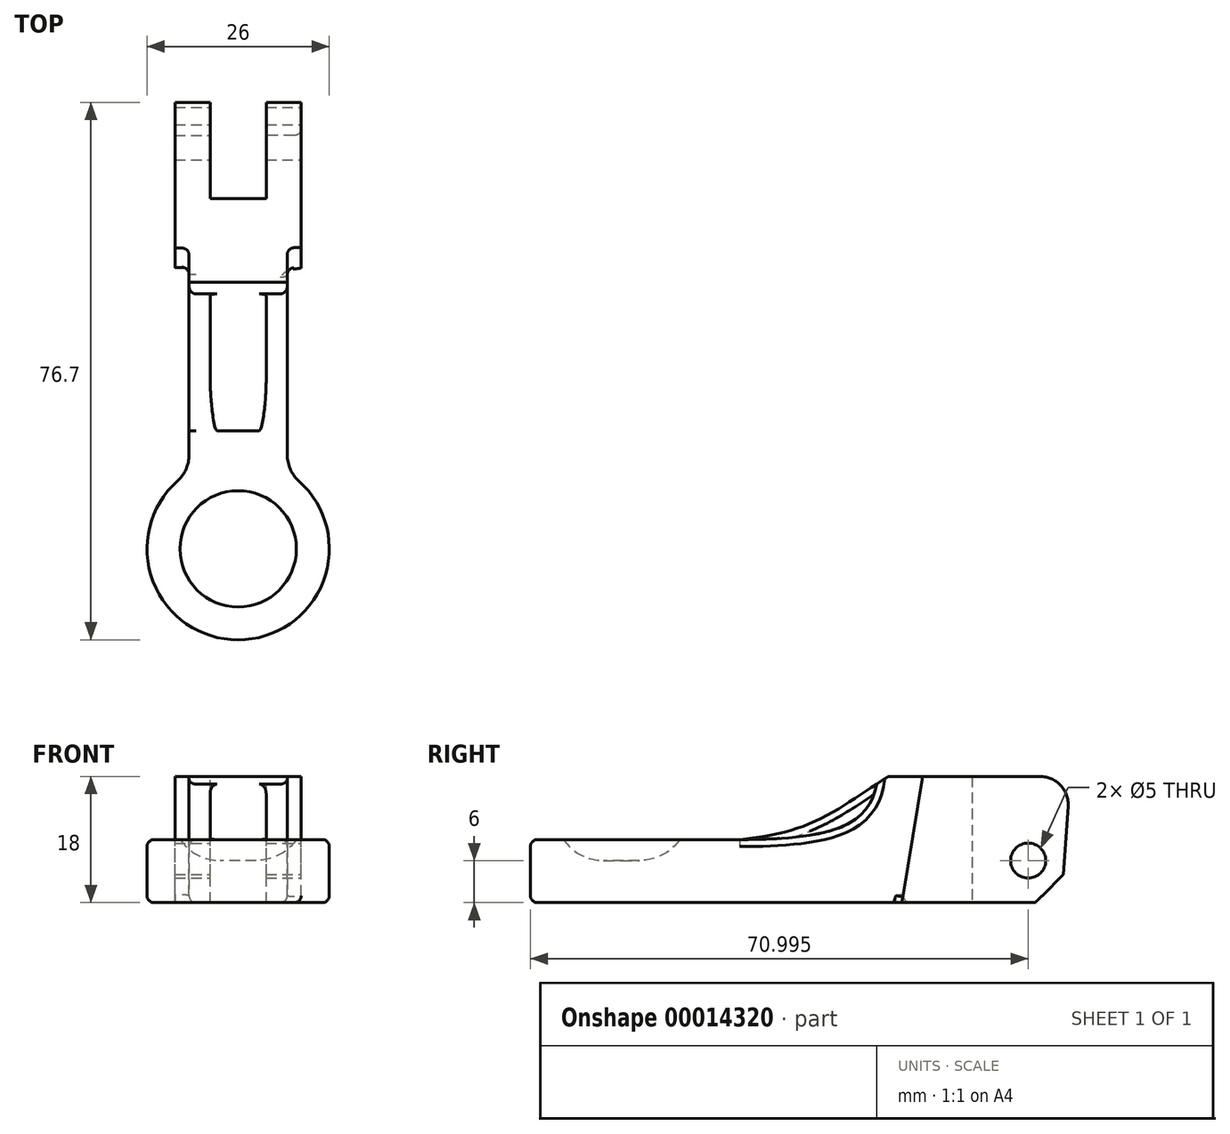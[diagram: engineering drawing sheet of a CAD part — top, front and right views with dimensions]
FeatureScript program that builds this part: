
annotation { "Feature Type Name" : "Feature", "Feature Type Description" : "" }
export const myFeature = defineFeature(function(context is Context, id is Id, definition is map)
    precondition{}
    {
        {
            var Q0;
            Q0=qCreatedBy(makeId("Top.planeOp"),FACE);
            var sketch = newSketch(context, id + "F0", { "sketchPlane" : qUnion([Q0])});
            skLineSegment(sketch, "E0.bottom", {"start": v(-82.63, 36.8) * mm, "end": v(-77.63, 36.8) * mm});
            skLineSegment(sketch, "E0.top", {"start": v(-82.63, 11.8) * mm, "end": v(-80.63, 11.8) * mm});
            skLineSegment(sketch, "E0.left", {"start": v(-82.63, 36.8) * mm, "end": v(-82.63, 11.8) * mm});
            skLineSegment(sketch, "E0.right", {"start": v(-64.63, 36.8) * mm, "end": v(-64.63, 11.8) * mm});
            skLineSegment(sketch, "E1.top", {"start": v(-77.63, 22.8) * mm, "end": v(-69.63, 22.8) * mm});
            skLineSegment(sketch, "E1.left", {"start": v(-77.63, 36.8) * mm, "end": v(-77.63, 22.8) * mm});
            skLineSegment(sketch, "E1.right", {"start": v(-69.63, 36.8) * mm, "end": v(-69.63, 22.8) * mm});
            skLineSegment(sketch, "E2.trimOffspring", {"start": v(-69.63, 36.8) * mm, "end": v(-64.63, 36.8) * mm});
            skLineSegment(sketch, "E3.left", {"start": v(-80.63, 11.8) * mm, "end": v(-80.63, -13.79) * mm});
            skLineSegment(sketch, "E3.right", {"start": v(-66.63, 11.8) * mm, "end": v(-66.63, -13.79) * mm});
            skArc(sketch, "E4", {"start": v(-82.3, -17.52) * mm, "mid": v(-73.63, -40.2) * mm, "end": v(-64.96, -17.52) * mm});
            skLineSegment(sketch, "E5", {"start": v(-73.63, 22.8) * mm, "end": v(-73.63, -62.63) * mm, "construction": true});
            skPoint(sketch, "E6.visualSharp", {"position": v(-66.63, -16.25) * mm});
            skArc(sketch, "E6.filletArc", {"start": v(-66.63, -13.79) * mm, "mid": v(-66.2, -15.83) * mm, "end": v(-64.96, -17.52) * mm});
            skPoint(sketch, "E7.visualSharp", {"position": v(-80.63, -16.25) * mm});
            skArc(sketch, "E7.filletArc", {"start": v(-82.3, -17.52) * mm, "mid": v(-81.07, -15.83) * mm, "end": v(-80.63, -13.79) * mm});
            skPoint(sketch, "E8.visualSharp", {"position": v(-64.63, 11.8) * mm});
            skLineSegment(sketch, "E8.filletArc", {"start": v(-64.63, 11.8) * mm, "end": v(-64.63, 11.8) * mm});
            skPoint(sketch, "E9.visualSharp", {"position": v(-82.63, 11.8) * mm});
            skLineSegment(sketch, "E9.filletArc", {"start": v(-82.63, 11.8) * mm, "end": v(-82.63, 11.8) * mm});
            skLineSegment(sketch, "E10.trimOffspring", {"start": v(-66.63, 11.8) * mm, "end": v(-64.63, 11.8) * mm});
            skPoint(sketch, "E11.visualSharp", {"position": v(-80.63, 11.8) * mm});
            skLineSegment(sketch, "E11.filletArc", {"start": v(-80.63, 11.8) * mm, "end": v(-80.63, 11.8) * mm});
            skPoint(sketch, "E12.visualSharp", {"position": v(-66.63, 11.8) * mm});
            skLineSegment(sketch, "E12.filletArc", {"start": v(-66.63, 11.8) * mm, "end": v(-66.63, 11.8) * mm});
            skCircle(sketch, "E13", {"center": v(-73.63, -27.2) * mm, "radius": 8.26 * mm});
            skSolve(sketch);
        }
        {
            var Q0;
            Q0 = qSketchRegion(id + "F0", true);
            var Q1;
            Q1=makeQuery(id+"F0.imprint","IMPRINT",FACE,{"disambiguationData":[TD([[makeQuery(id+"F0.imprint","IMPRINT",EDGE,{"derivedFrom":sQuery(id+"F0.wireOp",EDGE,"E13")}),1.0]])]});
            extrude(context, id + "F1", {"entities" : qUnion([Q0, Q1]), "depth" : 18 * mm});
        }
        {
            var Q0;
            Q0=qCreatedBy(makeId("Right.planeOp"),FACE);
            var sketch = newSketch(context, id + "F2", { "sketchPlane" : qUnion([Q0])});
            skLineSegment(sketch, "E14", {"start": v(-40.29, 25.83) * mm, "end": v(12.5, 25.83) * mm});
            skLineSegment(sketch, "E15", {"start": v(12.5, 25.83) * mm, "end": v(12.5, 19.02) * mm});
            skLineSegment(sketch, "E16", {"start": v(-10.36, 9) * mm, "end": v(-41.5, 9) * mm});
            skLineSegment(sketch, "E17", {"start": v(-41.5, 9) * mm, "end": v(-40.29, 25.83) * mm});
            skFitSpline(sketch, "E18", {"points": [v(-10.36, 9) * mm, v(12.5, 19.02) * mm], "startDerivative": vector(34.09, 3.12) * mm, "endDerivative": vector(25.68, 15.53) * mm});
            skSolve(sketch);
        }
        {
            var Q0;
            Q0 = qSketchRegion(id + "F2", true);
            extrude(context, id + "F3", {"entities" : qUnion([Q0]), "operationType" : NewBodyOperationType.REMOVE, "oppositeDirection" : true, "depth" : 125 * mm});
        }
        {
            var Q0;
            Q0=makeQuery(id+"F3.boolean.opBoolean","COPY",FACE,{"derivedFrom":makeQuery(id+"F3.opExtrude","SWEPT_FACE",FACE,{"disambiguationData":[OSD([sQuery(id+"F2.wireOp",EDGE,"E16")])]})});
            var sketch = newSketch(context, id + "F4", { "sketchPlane" : qUnion([Q0])});
            skCircle(sketch, "E19", {"center": v(-73.63, -27.2) * mm, "radius": 8.3 * mm});
            skSolve(sketch);
        }
        {
            var Q0;
            Q0 = qSketchRegion(id + "F4", true);
            extrude(context, id + "F5", {"entities" : qUnion([Q0]), "operationType" : NewBodyOperationType.REMOVE, "oppositeDirection" : true, "depth" : 3 * mm});
        }
        {
            var Q0;
            Q0=makeQuery(id+"F1.opExtrude","SWEPT_FACE",FACE,{"disambiguationData":[OSD([sQuery(id+"F0.wireOp",EDGE,"E0.right")])]});
            var sketch = newSketch(context, id + "F6", { "sketchPlane" : qUnion([Q0])});
            skCircle(sketch, "E20", {"center": v(30.8, 6) * mm, "radius": 2.5 * mm});
            skSolve(sketch);
        }
        {
            var Q0;
            Q0 = qSketchRegion(id + "F6", true);
            extrude(context, id + "F7", {"entities" : qUnion([Q0]), "operationType" : NewBodyOperationType.REMOVE, "oppositeDirection" : true, "depth" : 25 * mm});
        }
        {
            var Q0;
            Q0=makeQuery(id+"F1.opExtrude","SWEPT_FACE",FACE,{"disambiguationData":[OSD([sQuery(id+"F0.wireOp",EDGE,"E0.right")])]});
            var sketch = newSketch(context, id + "F8", { "sketchPlane" : qUnion([Q0])});
            skLineSegment(sketch, "E21", {"start": v(47.75, 30.34) * mm, "end": v(52.51, 30.34) * mm});
            skLineSegment(sketch, "E22", {"start": v(52.51, 30.34) * mm, "end": v(52.51, -1.5) * mm});
            skLineSegment(sketch, "E23", {"start": v(52.51, -1.5) * mm, "end": v(31.8, -1.5) * mm});
            skLineSegment(sketch, "E24", {"start": v(31.8, -1.5) * mm, "end": v(31.8, 0) * mm});
            skLineSegment(sketch, "E25", {"start": v(31.8, 0) * mm, "end": v(35.8, 0) * mm, "construction": true});
            skLineSegment(sketch, "E26", {"start": v(35.8, 0) * mm, "end": v(35.8, 4) * mm, "construction": true});
            skLineSegment(sketch, "E27", {"start": v(31.8, 0) * mm, "end": v(35.8, 4) * mm});
            skLineSegment(sketch, "E28", {"start": v(35.8, 4) * mm, "end": v(36.8, 18) * mm});
            skLineSegment(sketch, "E29", {"start": v(36.8, 18) * mm, "end": v(47.75, 30.34) * mm});
            skSolve(sketch);
        }
        {
            var Q0;
            Q0 = qSketchRegion(id + "F8", true);
            extrude(context, id + "F9", {"entities" : qUnion([Q0]), "operationType" : NewBodyOperationType.REMOVE, "oppositeDirection" : true, "depth" : 25 * mm});
        }
        {
            var Q0;
            Q0=makeQuery(id+"F1.opExtrude","SWEPT_FACE",FACE,{"disambiguationData":[OSD([sQuery(id+"F0.wireOp",EDGE,"E3.right")])]});
            var sketch = newSketch(context, id + "F10", { "sketchPlane" : qUnion([Q0])});
            skFitSpline(sketch, "E30", {"points": [v(-10.36, 9) * mm, v(9.18, 16.92) * mm], "startDerivative": vector(35.44, 0.16) * mm, "endDerivative": vector(3.26, 19.64) * mm});
            skLineSegment(sketch, "E31", {"start": v(9.18, 16.92) * mm, "end": v(-5.8, 16.92) * mm});
            skLineSegment(sketch, "E32", {"start": v(-5.8, 16.92) * mm, "end": v(-10.36, 9) * mm});
            skSolve(sketch);
        }
        {
            var Q0;
            Q0 = qSketchRegion(id + "F10", true);
            extrude(context, id + "F11", {"entities" : qUnion([Q0]), "operationType" : NewBodyOperationType.REMOVE, "oppositeDirection" : true, "depth" : 3 * mm});
        }
        {
            var Q0;
            Q0=makeQuery(id+"F1.opExtrude","SWEPT_FACE",FACE,{"disambiguationData":[OSD([sQuery(id+"F0.wireOp",EDGE,"E3.left")])]});
            var sketch = newSketch(context, id + "F12", { "sketchPlane" : qUnion([Q0])});
            skFitSpline(sketch, "E33", {"points": [v(-9.18, 16.92) * mm, v(10.36, 9) * mm], "startDerivative": vector(2.99, -19.1) * mm, "endDerivative": vector(36.23, -0.33) * mm});
            skLineSegment(sketch, "E34", {"start": v(-9.18, 16.92) * mm, "end": v(5.82, 16.92) * mm});
            skLineSegment(sketch, "E35", {"start": v(5.82, 16.92) * mm, "end": v(10.36, 9) * mm});
            skSolve(sketch);
        }
        {
            var Q0;
            Q0 = qSketchRegion(id + "F12", true);
            extrude(context, id + "F13", {"entities" : qUnion([Q0]), "operationType" : NewBodyOperationType.REMOVE, "oppositeDirection" : true, "depth" : 3 * mm});
        }
        {
            var Q0;
            Q0=makeQuery(id+"F1.opExtrude","SWEPT_FACE",FACE,{"disambiguationData":[OSD([sQuery(id+"F0.wireOp",EDGE,"E0.right")])]});
            var sketch = newSketch(context, id + "F14", { "sketchPlane" : qUnion([Q0])});
            skLineSegment(sketch, "E36", {"start": v(22.77, 0) * mm, "end": v(12.77, 0) * mm, "construction": true});
            skLineSegment(sketch, "E37", {"start": v(22.77, 0) * mm, "end": v(22.77, 17.98) * mm, "construction": true});
            skLineSegment(sketch, "E38", {"start": v(22.77, 17.98) * mm, "end": v(15.77, 17.98) * mm, "construction": true});
            skLineSegment(sketch, "E39", {"start": v(9.68, 20.3) * mm, "end": v(9.22, -2.99) * mm});
            skLineSegment(sketch, "E40", {"start": v(9.22, -2.99) * mm, "end": v(12.1, -2.99) * mm});
            skLineSegment(sketch, "E41", {"start": v(12.1, -2.99) * mm, "end": v(12.77, 0) * mm});
            skLineSegment(sketch, "E42", {"start": v(9.68, 20.3) * mm, "end": v(16.08, 19.87) * mm});
            skLineSegment(sketch, "E43", {"start": v(12.77, 0) * mm, "end": v(16.08, 19.87) * mm});
            skSolve(sketch);
        }
        {
            var Q0;
            Q0 = qSketchRegion(id + "F14", true);
            extrude(context, id + "F15", {"entities" : qUnion([Q0]), "operationType" : NewBodyOperationType.REMOVE, "oppositeDirection" : true, "depth" : 2 * mm});
        }
        {
            var Q0;
            Q0=makeQuery(id+"F1.opExtrude","SWEPT_FACE",FACE,{"disambiguationData":[OSD([sQuery(id+"F0.wireOp",EDGE,"E0.left")])]});
            var sketch = newSketch(context, id + "F16", { "sketchPlane" : qUnion([Q0])});
            skLineSegment(sketch, "E44", {"start": v(-12.8, 0) * mm, "end": v(-15.71, 18) * mm});
            skLineSegment(sketch, "E45", {"start": v(-15.71, 18) * mm, "end": v(-12.42, 21.29) * mm});
            skLineSegment(sketch, "E46", {"start": v(-12.42, 21.29) * mm, "end": v(-9.36, 20.22) * mm});
            skLineSegment(sketch, "E47", {"start": v(-9.36, 20.22) * mm, "end": v(-8.88, -2.86) * mm});
            skLineSegment(sketch, "E48", {"start": v(-8.88, -2.86) * mm, "end": v(-12.32, -2.93) * mm});
            skLineSegment(sketch, "E49", {"start": v(-12.32, -2.93) * mm, "end": v(-12.8, 0) * mm});
            skSolve(sketch);
        }
        {
            var Q0;
            Q0 = qSketchRegion(id + "F16", true);
            extrude(context, id + "F17", {"entities" : qUnion([Q0]), "operationType" : NewBodyOperationType.REMOVE, "oppositeDirection" : true, "depth" : 2 * mm});
        }
        {
            var Q0;
            Q0=makeQuery(id+"F5.boolean.opBoolean","COPY",EDGE,{"derivedFrom":makeQuery(id+"F5.opExtrude","CAP_EDGE",EDGE,{"disambiguationData":[OSD([sQuery(id+"F4.wireOp",EDGE,"E19")])],"isStart":false})});
            fillet(context, id + "F18", {"entities" : qUnion([Q0]), "radius" : 7 * mm, "tangentPropagation" : true, "allowEdgeOverflow" : false});
        }
        {
            var Q0;
            Q0=makeQuery(id+"F9.boolean.opBoolean","MERGE",EDGE,{"derivedFrom":[makeQuery(id+"F1.opExtrude","CAP_EDGE",EDGE,{"disambiguationData":[OSD([sQuery(id+"F0.wireOp",EDGE,"E0.bottom")])],"isStart":false}),makeQuery(id+"F9.opExtrude","SWEPT_EDGE",EDGE,{"disambiguationData":[OSD([sQuery(id+"F0.wireOp",EDGE,"E0.right"),sQuery(id+"F0.wireOp",EDGE,"E2.trimOffspring"),sQuery(id+"F8.wireOp",EDGE,"E28"),sQuery(id+"F8.wireOp",EDGE,"E29")])]})]});
            fillet(context, id + "F19", {"entities" : qUnion([Q0]), "radius" : 4 * mm, "tangentPropagation" : true, "allowEdgeOverflow" : false});
        }
        {
            var Q0;
            {var subQ0=sQuery(id+"F0.wireOp",EDGE,"E2.trimOffspring");Q0=makeQuery(id+"F9.boolean.opBoolean","MERGE",EDGE,{"derivedFrom":[makeQuery(id+"F1.opExtrude","CAP_EDGE",EDGE,{"disambiguationData":[OSD([subQ0])],"isStart":false}),makeQuery(id+"F9.opExtrude","SWEPT_EDGE",EDGE,{"disambiguationData":[OSD([sQuery(id+"F0.wireOp",EDGE,"E0.right"),subQ0,sQuery(id+"F8.wireOp",EDGE,"E28"),sQuery(id+"F8.wireOp",EDGE,"E29")])]})]});}
            fillet(context, id + "F20", {"entities" : qUnion([Q0]), "radius" : 4 * mm, "tangentPropagation" : true, "allowEdgeOverflow" : false});
        }
        {
            var Q0;
            Q0=makeQuery(id+"F17.boolean.opBoolean","COPY",EDGE,{"derivedFrom":makeQuery(id+"F17.opExtrude","CAP_EDGE",EDGE,{"disambiguationData":[OSD([sQuery(id+"F16.wireOp",EDGE,"E44")])],"isStart":true})});
            var Q1;
            Q1=makeQuery(id+"F17.boolean.opBoolean","COPY",EDGE,{"derivedFrom":makeQuery(id+"F17.opExtrude","CAP_EDGE",EDGE,{"disambiguationData":[OSD([sQuery(id+"F16.wireOp",EDGE,"E44")])],"isStart":false})});
            var Q2;
            Q2=makeQuery(id+"F3.boolean.opBoolean","INTERSECT",EDGE,{"derivedFrom":[makeQuery(id+"F1.opExtrude","SWEPT_FACE",FACE,{"disambiguationData":[OSD([sQuery(id+"F0.wireOp",EDGE,"E4")])]}),makeQuery(id+"F3.opExtrude","SWEPT_FACE",FACE,{"disambiguationData":[OSD([sQuery(id+"F2.wireOp",EDGE,"E16")])]})]});
            fillet(context, id + "F21", {"entities" : qUnion([Q0, Q1, Q2]), "radius" : 1 * mm, "tangentPropagation" : true, "allowEdgeOverflow" : false});
        }
        {
            var Q0;
            Q0=makeQuery(id+"F13.boolean.opBoolean","INTERSECT",EDGE,{"derivedFrom":[makeQuery(id+"F3.boolean.opBoolean","COPY",FACE,{"derivedFrom":makeQuery(id+"F3.opExtrude","SWEPT_FACE",FACE,{"disambiguationData":[OSD([sQuery(id+"F2.wireOp",EDGE,"E18")])]})}),makeQuery(id+"F13.opExtrude","CAP_FACE",FACE,{"disambiguationData":[OSD([sQuery(id+"F12.wireOp",EDGE,"E33"),sQuery(id+"F12.wireOp",EDGE,"E34"),sQuery(id+"F12.wireOp",EDGE,"E35")])],"isStart":false})]});
            var Q1;
            Q1=makeQuery(id+"F11.boolean.opBoolean","INTERSECT",EDGE,{"derivedFrom":[makeQuery(id+"F3.boolean.opBoolean","COPY",FACE,{"derivedFrom":makeQuery(id+"F3.opExtrude","SWEPT_FACE",FACE,{"disambiguationData":[OSD([sQuery(id+"F2.wireOp",EDGE,"E18")])]})}),makeQuery(id+"F11.opExtrude","CAP_FACE",FACE,{"disambiguationData":[OSD([sQuery(id+"F10.wireOp",EDGE,"E30"),sQuery(id+"F10.wireOp",EDGE,"E31"),sQuery(id+"F10.wireOp",EDGE,"E32")])],"isStart":false})]});
            fillet(context, id + "F22", {"entities" : qUnion([Q0, Q1]), "radius" : 1 * mm, "tangentPropagation" : true, "allowEdgeOverflow" : false});
        }
        {
            var Q0;
            Q0=makeQuery(id+"F1.opExtrude","CAP_EDGE",EDGE,{"disambiguationData":[OSD([sQuery(id+"F0.wireOp",EDGE,"E4")])],"isStart":true});
            fillet(context, id + "F23", {"entities" : qUnion([Q0]), "radius" : 1 * mm, "tangentPropagation" : true, "allowEdgeOverflow" : false});
        }
        {
            var Q0;
            Q0=makeQuery(id+"F15.boolean.opBoolean","COPY",EDGE,{"derivedFrom":makeQuery(id+"F15.opExtrude","CAP_EDGE",EDGE,{"disambiguationData":[OSD([sQuery(id+"F14.wireOp",EDGE,"45279244-bfe1-4c01-a6c2-df166d9699fa")])],"isStart":true})});
            var Q1;
            Q1=makeQuery(id+"F15.boolean.opBoolean","COPY",EDGE,{"derivedFrom":makeQuery(id+"F15.opExtrude","CAP_EDGE",EDGE,{"disambiguationData":[OSD([sQuery(id+"F14.wireOp",EDGE,"45279244-bfe1-4c01-a6c2-df166d9699fa")])],"isStart":false})});
            var Q2;
            Q2=makeQuery(id+"F1.opExtrude","CAP_EDGE",EDGE,{"disambiguationData":[OSD([sQuery(id+"F0.wireOp",EDGE,"E0.right")])],"isStart":true});
            var Q3;
            Q3=makeQuery(id+"F15.boolean.opBoolean","COPY",EDGE,{"derivedFrom":makeQuery(id+"F15.opExtrude","SWEPT_EDGE",EDGE,{"disambiguationData":[OSD([sQuery(id+"F0.wireOp",EDGE,"E0.right"),sQuery(id+"F14.wireOp",EDGE,"45279244-bfe1-4c01-a6c2-df166d9699fa"),sQuery(id+"F14.wireOp",EDGE,"E41")])]})});
            var Q4;
            Q4=makeQuery(id+"F15.boolean.opBoolean","COPY",EDGE,{"derivedFrom":makeQuery(id+"F15.opExtrude","CAP_EDGE",EDGE,{"disambiguationData":[OSD([sQuery(id+"F14.wireOp",EDGE,"E43")])],"isStart":true})});
            var Q5;
            Q5=makeQuery(id+"F15.boolean.opBoolean","COPY",EDGE,{"derivedFrom":makeQuery(id+"F15.opExtrude","CAP_EDGE",EDGE,{"disambiguationData":[OSD([sQuery(id+"F14.wireOp",EDGE,"E43")])],"isStart":false})});
            fillet(context, id + "F24", {"entities" : qUnion([Q0, Q1, Q2, Q3, Q4, Q5]), "radius" : 1 * mm, "tangentPropagation" : true, "allowEdgeOverflow" : false});
        }
    });
